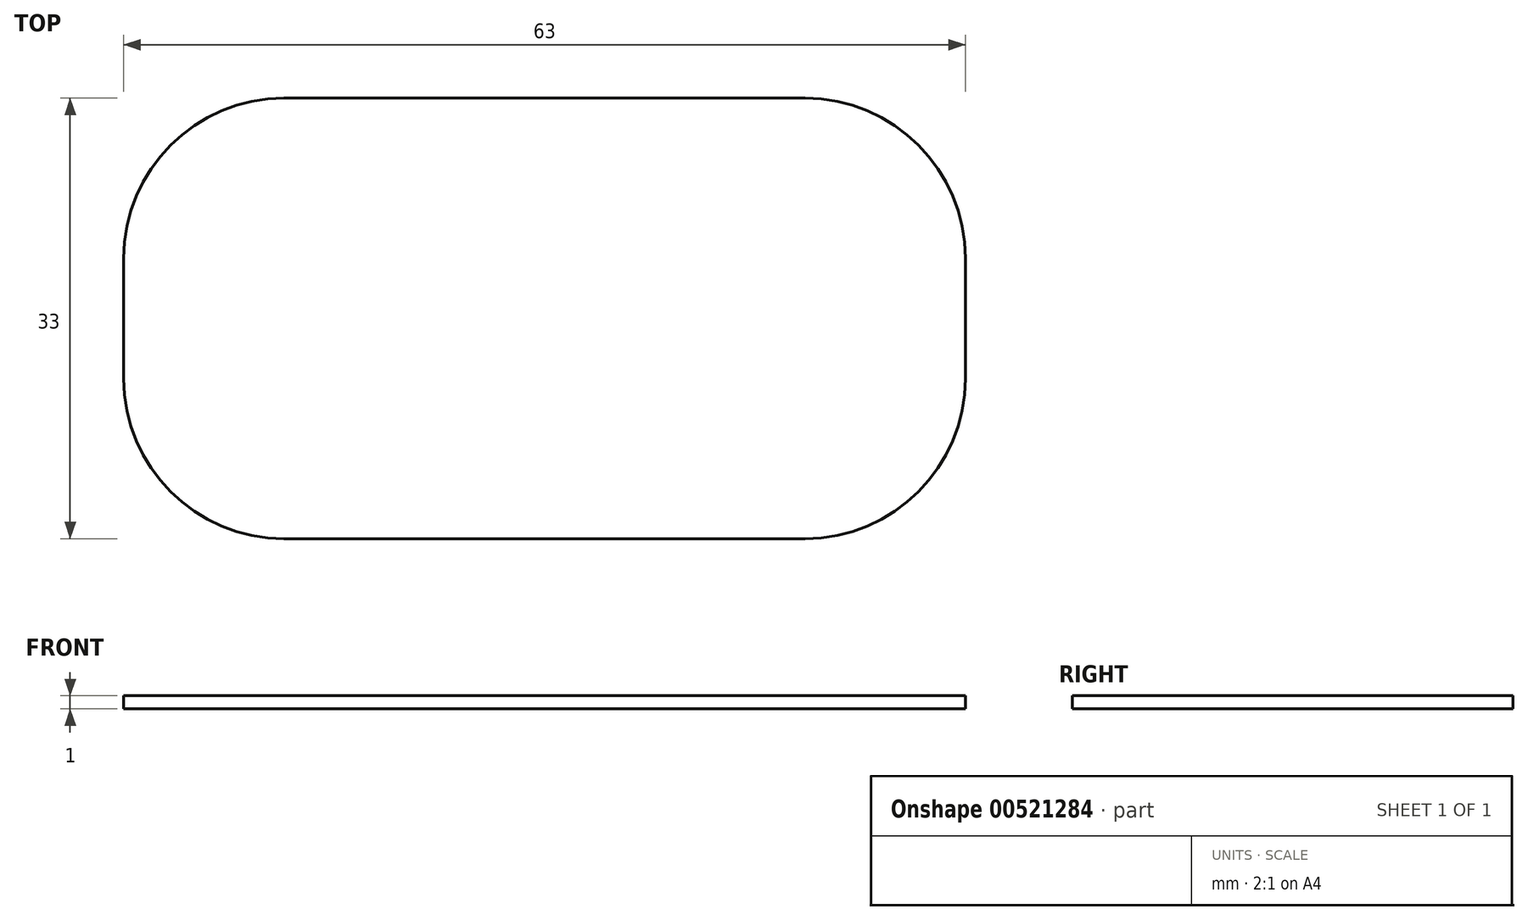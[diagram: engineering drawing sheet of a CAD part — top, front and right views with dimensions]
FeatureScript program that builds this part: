
annotation { "Feature Type Name" : "Feature", "Feature Type Description" : "" }
export const myFeature = defineFeature(function(context is Context, id is Id, definition is map)
    precondition{}
    {
        {
            var Q0;
            Q0=qCreatedBy(makeId("Top.planeOp"),FACE);
            var sketch = newSketch(context, id + "F0", { "sketchPlane" : qUnion([Q0])});
            skLineSegment(sketch, "E0.bottom", {"start": v(-19.5, 16.5) * mm, "end": v(19.5, 16.5) * mm});
            skLineSegment(sketch, "E0.top", {"start": v(-19.5, -16.5) * mm, "end": v(19.5, -16.5) * mm});
            skLineSegment(sketch, "E0.left", {"start": v(-31.5, 4.5) * mm, "end": v(-31.5, -4.5) * mm});
            skLineSegment(sketch, "E0.right", {"start": v(31.5, 4.5) * mm, "end": v(31.5, -4.5) * mm});
            skLineSegment(sketch, "E1", {"start": v(-31.5, -16.5) * mm, "end": v(31.5, 16.5) * mm});
            skPoint(sketch, "E2.visualSharp", {"position": v(-31.5, 16.5) * mm});
            skArc(sketch, "E2.filletArc", {"start": v(-19.5, 16.5) * mm, "mid": v(-27.99, 12.99) * mm, "end": v(-31.5, 4.5) * mm});
            skPoint(sketch, "E3.visualSharp", {"position": v(-31.5, -16.5) * mm});
            skArc(sketch, "E3.filletArc", {"start": v(-31.5, -4.5) * mm, "mid": v(-27.99, -12.99) * mm, "end": v(-19.5, -16.5) * mm});
            skPoint(sketch, "E4.visualSharp", {"position": v(31.5, -16.5) * mm});
            skArc(sketch, "E4.filletArc", {"start": v(19.5, -16.5) * mm, "mid": v(27.99, -12.99) * mm, "end": v(31.5, -4.5) * mm});
            skPoint(sketch, "E5.visualSharp", {"position": v(31.5, 16.5) * mm});
            skArc(sketch, "E5.filletArc", {"start": v(31.5, 4.5) * mm, "mid": v(27.99, 12.99) * mm, "end": v(19.5, 16.5) * mm});
            skSolve(sketch);
        }
        {
            var Q0;
            {var subQ6=sQuery(id+"F0.wireOp",EDGE,"E0.bottom");Q0=makeQuery(id+"F0.imprint","IMPRINT",FACE,{"disambiguationData":[TD([[makeQuery(id+"F0.imprint","IMPRINT",EDGE,{"derivedFrom":subQ6}),-1.0]])]});}
            var Q1;
            {var subQ1=sQuery(id+"F0.wireOp",EDGE,"E0.top");Q1=makeQuery(id+"F0.imprint","IMPRINT",FACE,{"disambiguationData":[TD([[makeQuery(id+"F0.imprint","IMPRINT",EDGE,{"derivedFrom":subQ1}),1.0]])]});}
            extrude(context, id + "F1", {"entities" : qUnion([Q0, Q1]), "depth" : 1 * mm, "offsetDistance" : 25 * mm});
        }
    });
